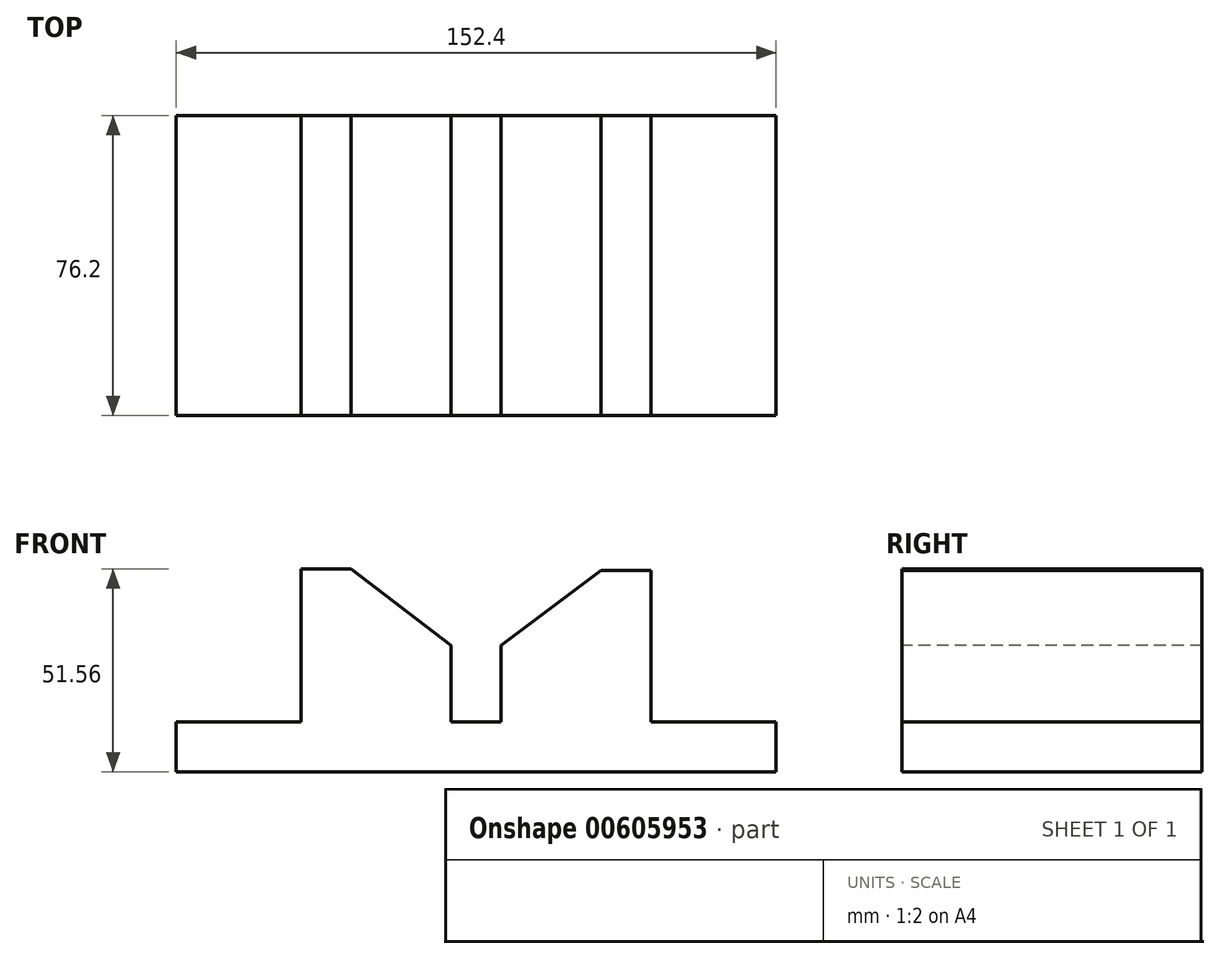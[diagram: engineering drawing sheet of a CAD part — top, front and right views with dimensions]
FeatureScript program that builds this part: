
annotation { "Feature Type Name" : "Feature", "Feature Type Description" : "" }
export const myFeature = defineFeature(function(context is Context, id is Id, definition is map)
    precondition{}
    {
        {
            var Q0;
            Q0=qCreatedBy(makeId("Front.planeOp"),FACE);
            var sketch = newSketch(context, id + "F0", { "sketchPlane" : qUnion([Q0])});
            skLineSegment(sketch, "E0", {"start": v(0, 0) * mm, "end": v(152.4, 0) * mm});
            skLineSegment(sketch, "E1", {"start": v(0, 0) * mm, "end": v(0, 12.7) * mm});
            skLineSegment(sketch, "E2", {"start": v(152.4, 12.7) * mm, "end": v(152.4, 0) * mm});
            skLineSegment(sketch, "E3", {"start": v(0, 12.7) * mm, "end": v(31.75, 12.7) * mm});
            skLineSegment(sketch, "E4", {"start": v(152.4, 12.7) * mm, "end": v(120.65, 12.7) * mm});
            skLineSegment(sketch, "E5", {"start": v(31.75, 12.7) * mm, "end": v(31.75, 51.56) * mm});
            skLineSegment(sketch, "E6", {"start": v(120.65, 12.7) * mm, "end": v(120.65, 51.18) * mm});
            skLineSegment(sketch, "E7", {"start": v(31.75, 51.56) * mm, "end": v(44.45, 51.56) * mm});
            skLineSegment(sketch, "E8", {"start": v(120.65, 51.18) * mm, "end": v(107.95, 51.18) * mm});
            skLineSegment(sketch, "E9", {"start": v(44.45, 51.56) * mm, "end": v(69.85, 32.13) * mm});
            skPoint(sketch, "E9.endSnap0", {"position": v(31.75, 32.13) * mm});
            skLineSegment(sketch, "E10", {"start": v(107.95, 51.18) * mm, "end": v(82.55, 32.13) * mm});
            skLineSegment(sketch, "E11", {"start": v(82.55, 32.13) * mm, "end": v(82.55, 12.7) * mm});
            skLineSegment(sketch, "E12", {"start": v(69.85, 32.13) * mm, "end": v(69.85, 12.7) * mm});
            skLineSegment(sketch, "E13", {"start": v(69.85, 12.7) * mm, "end": v(82.55, 12.7) * mm});
            skSolve(sketch);
        }
        {
            var Q0;
            Q0 = qSketchRegion(id + "F0", true);
            extrude(context, id + "F1", {"entities" : qUnion([Q0]), "oppositeDirection" : true, "depth" : 76.2 * mm, "offsetDistance" : 25.4 * mm});
        }
    });
